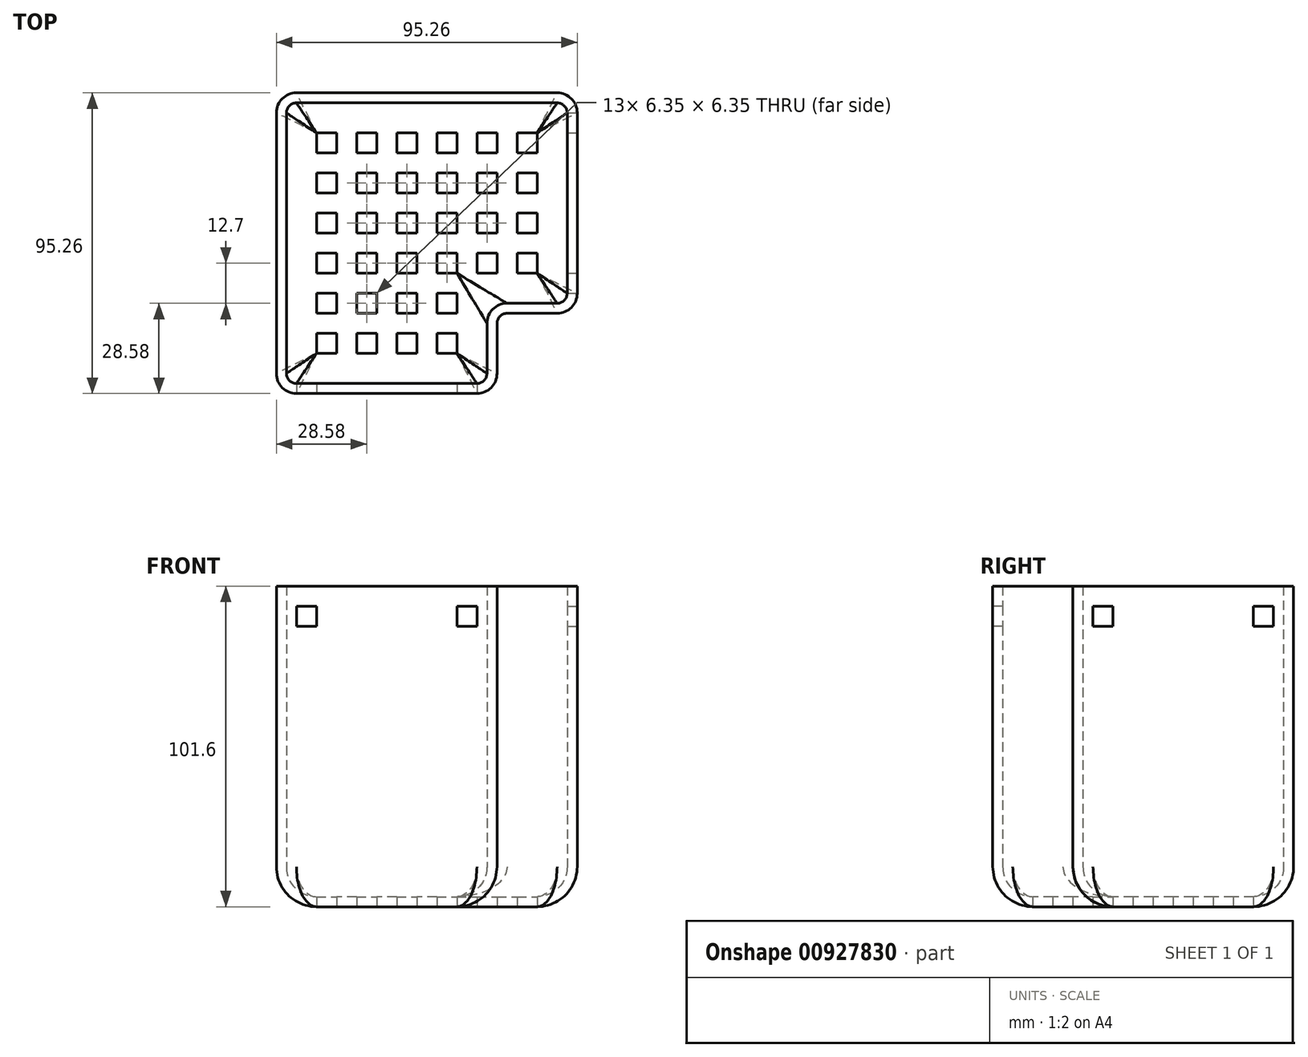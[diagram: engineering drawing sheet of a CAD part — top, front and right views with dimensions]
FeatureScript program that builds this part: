
annotation { "Feature Type Name" : "Feature", "Feature Type Description" : "" }
export const myFeature = defineFeature(function(context is Context, id is Id, definition is map)
    precondition{}
    {
        {
            var Q0;
            Q0=qCreatedBy(makeId("Top.planeOp"),FACE);
            var sketch = newSketch(context, id + "F0", { "sketchPlane" : qUnion([Q0])});
            skLineSegment(sketch, "E0.bottom", {"start": v(47.63, 47.63) * mm, "end": v(-47.63, 47.63) * mm});
            skLineSegment(sketch, "E0.top", {"start": v(22.23, -47.63) * mm, "end": v(-47.63, -47.63) * mm});
            skLineSegment(sketch, "E0.left", {"start": v(47.63, 47.63) * mm, "end": v(47.63, -22.23) * mm});
            skLineSegment(sketch, "E0.right", {"start": v(-47.63, 47.63) * mm, "end": v(-47.63, -47.63) * mm});
            skPoint(sketch, "E0.middle", {"position": v(0, 0) * mm});
            skLineSegment(sketch, "E1", {"start": v(22.23, -47.62) * mm, "end": v(22.23, -22.23) * mm});
            skLineSegment(sketch, "E2", {"start": v(22.23, -22.23) * mm, "end": v(47.62, -22.23) * mm});
            skPoint(sketch, "E3.orphan", {"position": v(47.63, -47.63) * mm});
            skLineSegment(sketch, "E4.0", {"start": v(44.45, 44.45) * mm, "end": v(44.45, -19.05) * mm});
            skLineSegment(sketch, "E4.1", {"start": v(-44.45, 44.45) * mm, "end": v(-44.45, -44.45) * mm});
            skLineSegment(sketch, "E4.2", {"start": v(19.05, -44.45) * mm, "end": v(-44.45, -44.45) * mm});
            skLineSegment(sketch, "E4.3", {"start": v(44.45, 44.45) * mm, "end": v(-44.45, 44.45) * mm});
            skLineSegment(sketch, "E4.4", {"start": v(19.05, -44.45) * mm, "end": v(19.05, -19.05) * mm});
            skLineSegment(sketch, "E4.5", {"start": v(19.05, -19.05) * mm, "end": v(44.45, -19.05) * mm});
            skSolve(sketch);
        }
        {
            var Q0;
            Q0 = qSketchRegion(id + "F0", true);
            extrude(context, id + "F1", {"entities" : qUnion([Q0]), "depth" : 101.6 * mm, "offsetDistance" : 25.4 * mm});
        }
        {
            var Q0;
            Q0=qCreatedBy(makeId("Top.planeOp"),FACE);
            var sketch = newSketch(context, id + "F2", { "sketchPlane" : qUnion([Q0])});
            skLineSegment(sketch, "E5.0.0", {"start": v(-47.63, -47.63) * mm, "end": v(22.23, -47.63) * mm});
            skLineSegment(sketch, "E5.0.1", {"start": v(22.23, -47.63) * mm, "end": v(22.23, -22.23) * mm});
            skLineSegment(sketch, "E5.0.2", {"start": v(22.23, -22.23) * mm, "end": v(47.63, -22.23) * mm});
            skLineSegment(sketch, "E5.0.3", {"start": v(47.63, -22.23) * mm, "end": v(47.63, 47.63) * mm});
            skLineSegment(sketch, "E5.0.4", {"start": v(47.63, 47.63) * mm, "end": v(-47.63, 47.63) * mm});
            skLineSegment(sketch, "E5.0.5", {"start": v(-47.63, 47.63) * mm, "end": v(-47.63, -47.63) * mm});
            skLineSegment(sketch, "E6.bottom", {"start": v(-34.93, 34.93) * mm, "end": v(-28.58, 34.93) * mm});
            skLineSegment(sketch, "E6.top", {"start": v(-34.93, 28.57) * mm, "end": v(-28.58, 28.57) * mm});
            skLineSegment(sketch, "E6.left", {"start": v(-34.93, 34.93) * mm, "end": v(-34.93, 28.58) * mm});
            skLineSegment(sketch, "E6.right", {"start": v(-28.58, 34.93) * mm, "end": v(-28.58, 28.57) * mm});
            skLineSegment(sketch, "E7.1.0.0", {"start": v(-22.23, 34.93) * mm, "end": v(-15.88, 34.93) * mm});
            skLineSegment(sketch, "E7.1.0.1", {"start": v(-22.23, 34.93) * mm, "end": v(-22.23, 28.58) * mm});
            skLineSegment(sketch, "E7.1.0.2", {"start": v(-15.88, 34.93) * mm, "end": v(-15.88, 28.57) * mm});
            skLineSegment(sketch, "E7.1.0.3", {"start": v(-22.23, 28.57) * mm, "end": v(-15.88, 28.57) * mm});
            skLineSegment(sketch, "E7.2.0.0", {"start": v(-9.53, 34.93) * mm, "end": v(-3.18, 34.93) * mm});
            skLineSegment(sketch, "E7.2.0.1", {"start": v(-9.53, 34.93) * mm, "end": v(-9.53, 28.58) * mm});
            skLineSegment(sketch, "E7.2.0.2", {"start": v(-3.18, 34.93) * mm, "end": v(-3.18, 28.57) * mm});
            skLineSegment(sketch, "E7.2.0.3", {"start": v(-9.53, 28.58) * mm, "end": v(-3.18, 28.58) * mm});
            skLineSegment(sketch, "E7.direction1", {"start": v(-34.93, 28.58) * mm, "end": v(-22.23, 28.58) * mm, "construction": true});
            skLineSegment(sketch, "E8.0.3.0", {"start": v(3.17, 34.93) * mm, "end": v(9.52, 34.93) * mm});
            skLineSegment(sketch, "E8.3.3.0", {"start": v(3.17, 34.93) * mm, "end": v(3.17, 28.58) * mm});
            skLineSegment(sketch, "E8.6.3.0", {"start": v(9.52, 34.93) * mm, "end": v(9.52, 28.57) * mm});
            skLineSegment(sketch, "E8.9.3.0", {"start": v(3.17, 28.58) * mm, "end": v(9.52, 28.58) * mm});
            skLineSegment(sketch, "E8.0.4.0", {"start": v(15.87, 34.93) * mm, "end": v(22.22, 34.93) * mm});
            skLineSegment(sketch, "E8.3.4.0", {"start": v(15.87, 34.93) * mm, "end": v(15.87, 28.58) * mm});
            skLineSegment(sketch, "E8.6.4.0", {"start": v(22.22, 34.93) * mm, "end": v(22.22, 28.57) * mm});
            skLineSegment(sketch, "E8.9.4.0", {"start": v(15.87, 28.58) * mm, "end": v(22.22, 28.58) * mm});
            skLineSegment(sketch, "E8.0.5.0", {"start": v(28.57, 34.93) * mm, "end": v(34.92, 34.93) * mm});
            skLineSegment(sketch, "E8.3.5.0", {"start": v(28.57, 34.93) * mm, "end": v(28.57, 28.58) * mm});
            skLineSegment(sketch, "E8.6.5.0", {"start": v(34.92, 34.93) * mm, "end": v(34.92, 28.57) * mm});
            skLineSegment(sketch, "E8.9.5.0", {"start": v(28.57, 28.58) * mm, "end": v(34.92, 28.58) * mm});
            skLineSegment(sketch, "E9.0.1.0", {"start": v(-34.93, 15.88) * mm, "end": v(-22.23, 15.88) * mm, "construction": true});
            skLineSegment(sketch, "E9.0.1.1", {"start": v(-22.23, 15.87) * mm, "end": v(-15.88, 15.87) * mm});
            skLineSegment(sketch, "E9.0.1.2", {"start": v(-28.58, 22.23) * mm, "end": v(-28.58, 15.87) * mm});
            skLineSegment(sketch, "E9.0.1.3", {"start": v(-22.23, 22.23) * mm, "end": v(-22.23, 15.88) * mm});
            skLineSegment(sketch, "E9.0.1.4", {"start": v(3.17, 22.23) * mm, "end": v(9.52, 22.23) * mm});
            skLineSegment(sketch, "E9.0.1.5", {"start": v(-15.88, 22.23) * mm, "end": v(-15.88, 15.87) * mm});
            skLineSegment(sketch, "E9.0.1.6", {"start": v(15.87, 15.88) * mm, "end": v(22.22, 15.88) * mm});
            skLineSegment(sketch, "E9.0.1.7", {"start": v(-34.93, 22.23) * mm, "end": v(-28.58, 22.23) * mm});
            skLineSegment(sketch, "E9.0.1.8", {"start": v(9.52, 22.23) * mm, "end": v(9.52, 15.87) * mm});
            skLineSegment(sketch, "E9.0.1.9", {"start": v(34.92, 22.23) * mm, "end": v(34.92, 15.87) * mm});
            skLineSegment(sketch, "E9.0.1.10", {"start": v(15.87, 22.23) * mm, "end": v(22.22, 22.23) * mm});
            skLineSegment(sketch, "E9.0.1.11", {"start": v(22.22, 22.23) * mm, "end": v(22.22, 15.87) * mm});
            skLineSegment(sketch, "E9.0.1.12", {"start": v(28.57, 22.23) * mm, "end": v(34.92, 22.23) * mm});
            skLineSegment(sketch, "E9.0.1.13", {"start": v(-34.93, 22.23) * mm, "end": v(-34.93, 15.88) * mm});
            skLineSegment(sketch, "E9.0.1.14", {"start": v(-22.23, 22.23) * mm, "end": v(-15.88, 22.23) * mm});
            skLineSegment(sketch, "E9.0.1.15", {"start": v(15.87, 22.23) * mm, "end": v(15.87, 15.88) * mm});
            skLineSegment(sketch, "E9.0.1.16", {"start": v(28.57, 15.88) * mm, "end": v(34.92, 15.88) * mm});
            skLineSegment(sketch, "E9.0.1.17", {"start": v(3.17, 22.23) * mm, "end": v(3.17, 15.88) * mm});
            skLineSegment(sketch, "E9.0.1.18", {"start": v(3.17, 15.88) * mm, "end": v(9.52, 15.88) * mm});
            skLineSegment(sketch, "E9.0.1.19", {"start": v(-9.53, 22.23) * mm, "end": v(-9.53, 15.88) * mm});
            skLineSegment(sketch, "E9.0.1.20", {"start": v(28.57, 22.23) * mm, "end": v(28.57, 15.88) * mm});
            skLineSegment(sketch, "E9.0.1.21", {"start": v(-3.18, 22.23) * mm, "end": v(-3.18, 15.87) * mm});
            skLineSegment(sketch, "E9.0.1.22", {"start": v(-9.53, 22.23) * mm, "end": v(-3.18, 22.23) * mm});
            skLineSegment(sketch, "E9.0.1.23", {"start": v(-9.53, 15.88) * mm, "end": v(-3.18, 15.88) * mm});
            skLineSegment(sketch, "E9.0.1.24", {"start": v(-34.93, 15.87) * mm, "end": v(-28.58, 15.87) * mm});
            skLineSegment(sketch, "E9.0.2.0", {"start": v(-34.93, 3.18) * mm, "end": v(-22.23, 3.18) * mm, "construction": true});
            skLineSegment(sketch, "E9.0.2.1", {"start": v(-22.23, 3.17) * mm, "end": v(-15.88, 3.17) * mm});
            skLineSegment(sketch, "E9.0.2.2", {"start": v(-28.58, 9.53) * mm, "end": v(-28.58, 3.17) * mm});
            skLineSegment(sketch, "E9.0.2.3", {"start": v(-22.23, 9.53) * mm, "end": v(-22.23, 3.18) * mm});
            skLineSegment(sketch, "E9.0.2.4", {"start": v(3.17, 9.53) * mm, "end": v(9.52, 9.53) * mm});
            skLineSegment(sketch, "E9.0.2.5", {"start": v(-15.88, 9.53) * mm, "end": v(-15.88, 3.17) * mm});
            skLineSegment(sketch, "E9.0.2.6", {"start": v(15.87, 3.18) * mm, "end": v(22.22, 3.18) * mm});
            skLineSegment(sketch, "E9.0.2.7", {"start": v(-34.93, 9.53) * mm, "end": v(-28.58, 9.53) * mm});
            skLineSegment(sketch, "E9.0.2.8", {"start": v(9.52, 9.53) * mm, "end": v(9.52, 3.17) * mm});
            skLineSegment(sketch, "E9.0.2.9", {"start": v(34.92, 9.53) * mm, "end": v(34.92, 3.17) * mm});
            skLineSegment(sketch, "E9.0.2.10", {"start": v(15.87, 9.53) * mm, "end": v(22.22, 9.53) * mm});
            skLineSegment(sketch, "E9.0.2.11", {"start": v(22.22, 9.53) * mm, "end": v(22.22, 3.17) * mm});
            skLineSegment(sketch, "E9.0.2.12", {"start": v(28.57, 9.53) * mm, "end": v(34.92, 9.53) * mm});
            skLineSegment(sketch, "E9.0.2.13", {"start": v(-34.93, 9.53) * mm, "end": v(-34.93, 3.18) * mm});
            skLineSegment(sketch, "E9.0.2.14", {"start": v(-22.23, 9.53) * mm, "end": v(-15.88, 9.53) * mm});
            skLineSegment(sketch, "E9.0.2.15", {"start": v(15.87, 9.53) * mm, "end": v(15.87, 3.18) * mm});
            skLineSegment(sketch, "E9.0.2.16", {"start": v(28.57, 3.18) * mm, "end": v(34.92, 3.18) * mm});
            skLineSegment(sketch, "E9.0.2.17", {"start": v(3.17, 9.53) * mm, "end": v(3.17, 3.18) * mm});
            skLineSegment(sketch, "E9.0.2.18", {"start": v(3.17, 3.18) * mm, "end": v(9.52, 3.18) * mm});
            skLineSegment(sketch, "E9.0.2.19", {"start": v(-9.53, 9.53) * mm, "end": v(-9.53, 3.18) * mm});
            skLineSegment(sketch, "E9.0.2.20", {"start": v(28.57, 9.53) * mm, "end": v(28.57, 3.18) * mm});
            skLineSegment(sketch, "E9.0.2.21", {"start": v(-3.18, 9.53) * mm, "end": v(-3.18, 3.17) * mm});
            skLineSegment(sketch, "E9.0.2.22", {"start": v(-9.53, 9.53) * mm, "end": v(-3.18, 9.53) * mm});
            skLineSegment(sketch, "E9.0.2.23", {"start": v(-9.53, 3.18) * mm, "end": v(-3.18, 3.18) * mm});
            skLineSegment(sketch, "E9.0.2.24", {"start": v(-34.93, 3.17) * mm, "end": v(-28.58, 3.17) * mm});
            skLineSegment(sketch, "E9.0.3.0", {"start": v(-34.93, -9.52) * mm, "end": v(-22.23, -9.52) * mm, "construction": true});
            skLineSegment(sketch, "E9.0.3.1", {"start": v(-22.23, -9.53) * mm, "end": v(-15.88, -9.52) * mm});
            skLineSegment(sketch, "E9.0.3.2", {"start": v(-28.58, -3.17) * mm, "end": v(-28.58, -9.53) * mm});
            skLineSegment(sketch, "E9.0.3.3", {"start": v(-22.23, -3.17) * mm, "end": v(-22.23, -9.52) * mm});
            skLineSegment(sketch, "E9.0.3.4", {"start": v(3.17, -3.17) * mm, "end": v(9.52, -3.17) * mm});
            skLineSegment(sketch, "E9.0.3.5", {"start": v(-15.88, -3.17) * mm, "end": v(-15.88, -9.53) * mm});
            skLineSegment(sketch, "E9.0.3.6", {"start": v(15.87, -9.52) * mm, "end": v(22.22, -9.52) * mm});
            skLineSegment(sketch, "E9.0.3.7", {"start": v(-34.93, -3.17) * mm, "end": v(-28.58, -3.17) * mm});
            skLineSegment(sketch, "E9.0.3.8", {"start": v(9.52, -3.17) * mm, "end": v(9.52, -9.53) * mm});
            skLineSegment(sketch, "E9.0.3.9", {"start": v(34.92, -3.17) * mm, "end": v(34.92, -9.53) * mm});
            skLineSegment(sketch, "E9.0.3.10", {"start": v(15.87, -3.17) * mm, "end": v(22.22, -3.17) * mm});
            skLineSegment(sketch, "E9.0.3.11", {"start": v(22.22, -3.17) * mm, "end": v(22.22, -9.53) * mm});
            skLineSegment(sketch, "E9.0.3.12", {"start": v(28.57, -3.17) * mm, "end": v(34.92, -3.17) * mm});
            skLineSegment(sketch, "E9.0.3.13", {"start": v(-34.93, -3.17) * mm, "end": v(-34.93, -9.52) * mm});
            skLineSegment(sketch, "E9.0.3.14", {"start": v(-22.23, -3.17) * mm, "end": v(-15.88, -3.17) * mm});
            skLineSegment(sketch, "E9.0.3.15", {"start": v(15.87, -3.17) * mm, "end": v(15.87, -9.52) * mm});
            skLineSegment(sketch, "E9.0.3.16", {"start": v(28.57, -9.52) * mm, "end": v(34.92, -9.52) * mm});
            skLineSegment(sketch, "E9.0.3.17", {"start": v(3.17, -3.17) * mm, "end": v(3.17, -9.52) * mm});
            skLineSegment(sketch, "E9.0.3.18", {"start": v(3.17, -9.52) * mm, "end": v(9.52, -9.52) * mm});
            skLineSegment(sketch, "E9.0.3.19", {"start": v(-9.53, -3.17) * mm, "end": v(-9.53, -9.52) * mm});
            skLineSegment(sketch, "E9.0.3.20", {"start": v(28.57, -3.17) * mm, "end": v(28.57, -9.52) * mm});
            skLineSegment(sketch, "E9.0.3.21", {"start": v(-3.18, -3.17) * mm, "end": v(-3.18, -9.53) * mm});
            skLineSegment(sketch, "E9.0.3.22", {"start": v(-9.53, -3.17) * mm, "end": v(-3.18, -3.17) * mm});
            skLineSegment(sketch, "E9.0.3.23", {"start": v(-9.53, -9.52) * mm, "end": v(-3.18, -9.52) * mm});
            skLineSegment(sketch, "E9.0.3.24", {"start": v(-34.93, -9.53) * mm, "end": v(-28.58, -9.53) * mm});
            skLineSegment(sketch, "E9.0.4.0", {"start": v(-34.93, -22.22) * mm, "end": v(-22.23, -22.22) * mm, "construction": true});
            skLineSegment(sketch, "E9.0.4.1", {"start": v(-22.23, -22.23) * mm, "end": v(-15.88, -22.23) * mm});
            skLineSegment(sketch, "E9.0.4.2", {"start": v(-28.58, -15.87) * mm, "end": v(-28.58, -22.23) * mm});
            skLineSegment(sketch, "E9.0.4.3", {"start": v(-22.23, -15.87) * mm, "end": v(-22.23, -22.22) * mm});
            skLineSegment(sketch, "E9.0.4.4", {"start": v(3.17, -15.87) * mm, "end": v(9.52, -15.87) * mm});
            skLineSegment(sketch, "E9.0.4.5", {"start": v(-15.88, -15.87) * mm, "end": v(-15.88, -22.23) * mm});
            skLineSegment(sketch, "E9.0.4.7", {"start": v(-34.93, -15.87) * mm, "end": v(-28.58, -15.87) * mm});
            skLineSegment(sketch, "E9.0.4.8", {"start": v(9.52, -15.87) * mm, "end": v(9.52, -22.23) * mm});
            skLineSegment(sketch, "E9.0.4.13", {"start": v(-34.93, -15.87) * mm, "end": v(-34.93, -22.22) * mm});
            skLineSegment(sketch, "E9.0.4.14", {"start": v(-22.23, -15.87) * mm, "end": v(-15.88, -15.87) * mm});
            skLineSegment(sketch, "E9.0.4.17", {"start": v(3.17, -15.87) * mm, "end": v(3.17, -22.22) * mm});
            skLineSegment(sketch, "E9.0.4.18", {"start": v(3.17, -22.22) * mm, "end": v(9.52, -22.22) * mm});
            skLineSegment(sketch, "E9.0.4.19", {"start": v(-9.53, -15.87) * mm, "end": v(-9.53, -22.22) * mm});
            skLineSegment(sketch, "E9.0.4.21", {"start": v(-3.18, -15.87) * mm, "end": v(-3.18, -22.23) * mm});
            skLineSegment(sketch, "E9.0.4.22", {"start": v(-9.53, -15.87) * mm, "end": v(-3.18, -15.87) * mm});
            skLineSegment(sketch, "E9.0.4.23", {"start": v(-9.53, -22.22) * mm, "end": v(-3.18, -22.22) * mm});
            skLineSegment(sketch, "E9.0.4.24", {"start": v(-34.93, -22.23) * mm, "end": v(-28.58, -22.23) * mm});
            skLineSegment(sketch, "E9.0.5.0", {"start": v(-34.93, -34.92) * mm, "end": v(-22.23, -34.92) * mm, "construction": true});
            skLineSegment(sketch, "E9.0.5.1", {"start": v(-22.23, -34.93) * mm, "end": v(-15.88, -34.93) * mm});
            skLineSegment(sketch, "E9.0.5.2", {"start": v(-28.58, -28.57) * mm, "end": v(-28.58, -34.93) * mm});
            skLineSegment(sketch, "E9.0.5.3", {"start": v(-22.23, -28.57) * mm, "end": v(-22.23, -34.92) * mm});
            skLineSegment(sketch, "E9.0.5.4", {"start": v(3.17, -28.57) * mm, "end": v(9.52, -28.57) * mm});
            skLineSegment(sketch, "E9.0.5.5", {"start": v(-15.88, -28.57) * mm, "end": v(-15.88, -34.93) * mm});
            skLineSegment(sketch, "E9.0.5.7", {"start": v(-34.93, -28.57) * mm, "end": v(-28.58, -28.57) * mm});
            skLineSegment(sketch, "E9.0.5.8", {"start": v(9.52, -28.57) * mm, "end": v(9.52, -34.93) * mm});
            skLineSegment(sketch, "E9.0.5.13", {"start": v(-34.93, -28.57) * mm, "end": v(-34.93, -34.92) * mm});
            skLineSegment(sketch, "E9.0.5.14", {"start": v(-22.23, -28.57) * mm, "end": v(-15.88, -28.57) * mm});
            skLineSegment(sketch, "E9.0.5.17", {"start": v(3.17, -28.57) * mm, "end": v(3.17, -34.92) * mm});
            skLineSegment(sketch, "E9.0.5.18", {"start": v(3.17, -34.92) * mm, "end": v(9.52, -34.92) * mm});
            skLineSegment(sketch, "E9.0.5.19", {"start": v(-9.53, -28.57) * mm, "end": v(-9.53, -34.92) * mm});
            skLineSegment(sketch, "E9.0.5.21", {"start": v(-3.18, -28.57) * mm, "end": v(-3.18, -34.93) * mm});
            skLineSegment(sketch, "E9.0.5.22", {"start": v(-9.53, -28.57) * mm, "end": v(-3.18, -28.57) * mm});
            skLineSegment(sketch, "E9.0.5.23", {"start": v(-9.53, -34.92) * mm, "end": v(-3.18, -34.92) * mm});
            skLineSegment(sketch, "E9.0.5.24", {"start": v(-34.93, -34.93) * mm, "end": v(-28.58, -34.93) * mm});
            skLineSegment(sketch, "E9.direction1", {"start": v(-34.93, 28.57) * mm, "end": v(-9.53, 28.57) * mm, "construction": true});
            skLineSegment(sketch, "E9.direction2", {"start": v(-34.93, 28.57) * mm, "end": v(-34.93, 15.87) * mm, "construction": true});
            skSolve(sketch);
        }
        {
            var Q0;
            Q0=makeQuery(id+"F2.imprint","IMPRINT",FACE,{"disambiguationData":[TD([[makeQuery(id+"F2.imprint","IMPRINT",EDGE,{"derivedFrom":sQuery(id+"F2.wireOp",EDGE,"E5.0.0")}),1.0]])]});
            extrude(context, id + "F3", {"entities" : qUnion([Q0]), "operationType" : NewBodyOperationType.ADD, "depth" : 3.17 * mm, "offsetDistance" : 25.4 * mm});
        }
        {
            var Q0;
            Q0=makeQuery(id+"F1.opExtrude","SWEPT_FACE",FACE,{"disambiguationData":[OSD([sQuery(id+"F0.wireOp",EDGE,"E0.top")])]});
            var sketch = newSketch(context, id + "F4", { "sketchPlane" : qUnion([Q0])});
            skLineSegment(sketch, "E10.bottom", {"start": v(-41.28, 95.25) * mm, "end": v(-34.93, 95.25) * mm});
            skLineSegment(sketch, "E10.top", {"start": v(-41.28, 88.9) * mm, "end": v(-34.93, 88.9) * mm});
            skLineSegment(sketch, "E10.left", {"start": v(-41.28, 95.25) * mm, "end": v(-41.28, 88.9) * mm});
            skLineSegment(sketch, "E10.right", {"start": v(-34.93, 95.25) * mm, "end": v(-34.93, 88.9) * mm});
            skLineSegment(sketch, "E11.bottom", {"start": v(15.88, 95.25) * mm, "end": v(9.53, 95.25) * mm});
            skLineSegment(sketch, "E11.top", {"start": v(15.88, 88.9) * mm, "end": v(9.53, 88.9) * mm});
            skLineSegment(sketch, "E11.left", {"start": v(15.88, 95.25) * mm, "end": v(15.88, 88.9) * mm});
            skLineSegment(sketch, "E11.right", {"start": v(9.53, 95.25) * mm, "end": v(9.53, 88.9) * mm});
            skSolve(sketch);
        }
        {
            var Q0;
            Q0 = qSketchRegion(id + "F4", true);
            extrude(context, id + "F5", {"entities" : qUnion([Q0]), "operationType" : NewBodyOperationType.REMOVE, "oppositeDirection" : true, "depth" : 25.4 * mm, "offsetDistance" : 25.4 * mm});
        }
        {
            var Q0;
            Q0=makeQuery(id+"F1.opExtrude","SWEPT_FACE",FACE,{"disambiguationData":[OSD([sQuery(id+"F0.wireOp",EDGE,"E0.left")])]});
            var sketch = newSketch(context, id + "F6", { "sketchPlane" : qUnion([Q0])});
            skLineSegment(sketch, "E12.bottom", {"start": v(41.28, 95.25) * mm, "end": v(34.93, 95.25) * mm});
            skLineSegment(sketch, "E12.top", {"start": v(41.28, 88.9) * mm, "end": v(34.93, 88.9) * mm});
            skLineSegment(sketch, "E12.left", {"start": v(41.28, 95.25) * mm, "end": v(41.28, 88.9) * mm});
            skLineSegment(sketch, "E12.right", {"start": v(34.93, 95.25) * mm, "end": v(34.93, 88.9) * mm});
            skLineSegment(sketch, "E13.bottom", {"start": v(-15.88, 95.25) * mm, "end": v(-9.53, 95.25) * mm});
            skLineSegment(sketch, "E13.top", {"start": v(-15.88, 88.9) * mm, "end": v(-9.53, 88.9) * mm});
            skLineSegment(sketch, "E13.left", {"start": v(-15.88, 95.25) * mm, "end": v(-15.88, 88.9) * mm});
            skLineSegment(sketch, "E13.right", {"start": v(-9.53, 95.25) * mm, "end": v(-9.53, 88.9) * mm});
            skSolve(sketch);
        }
        {
            var Q0;
            Q0 = qSketchRegion(id + "F6", true);
            extrude(context, id + "F7", {"entities" : qUnion([Q0]), "operationType" : NewBodyOperationType.REMOVE, "oppositeDirection" : true, "depth" : 25.4 * mm, "offsetDistance" : 25.4 * mm});
        }
        {
            var Q0;
            Q0=makeQuery(id+"F3.boolean.opBoolean","INTERSECT",EDGE,{"derivedFrom":[makeQuery(id+"F1.opExtrude","SWEPT_FACE",FACE,{"disambiguationData":[OSD([sQuery(id+"F0.wireOp",EDGE,"E4.3")])]}),makeQuery(id+"F3.opExtrude","CAP_FACE",FACE,{"disambiguationData":[OSD([sQuery(id+"F2.wireOp",EDGE,"E5.0.0"),sQuery(id+"F2.wireOp",EDGE,"E5.0.1"),sQuery(id+"F2.wireOp",EDGE,"E5.0.2"),sQuery(id+"F2.wireOp",EDGE,"E5.0.3"),sQuery(id+"F2.wireOp",EDGE,"E5.0.4"),sQuery(id+"F2.wireOp",EDGE,"E5.0.5"),sQuery(id+"F2.wireOp",EDGE,"E6.bottom"),sQuery(id+"F2.wireOp",EDGE,"E6.top"),sQuery(id+"F2.wireOp",EDGE,"E6.left"),sQuery(id+"F2.wireOp",EDGE,"E6.right"),sQuery(id+"F2.wireOp",EDGE,"E7.1.0.0"),sQuery(id+"F2.wireOp",EDGE,"E7.1.0.1"),sQuery(id+"F2.wireOp",EDGE,"E7.1.0.2"),sQuery(id+"F2.wireOp",EDGE,"E7.1.0.3"),sQuery(id+"F2.wireOp",EDGE,"E7.2.0.0"),sQuery(id+"F2.wireOp",EDGE,"E7.2.0.1"),sQuery(id+"F2.wireOp",EDGE,"E7.2.0.2"),sQuery(id+"F2.wireOp",EDGE,"E7.2.0.3"),sQuery(id+"F2.wireOp",EDGE,"E8.0.3.0"),sQuery(id+"F2.wireOp",EDGE,"E8.3.3.0"),sQuery(id+"F2.wireOp",EDGE,"E8.6.3.0"),sQuery(id+"F2.wireOp",EDGE,"E8.9.3.0"),sQuery(id+"F2.wireOp",EDGE,"E8.0.4.0"),sQuery(id+"F2.wireOp",EDGE,"E8.3.4.0"),sQuery(id+"F2.wireOp",EDGE,"E8.6.4.0"),sQuery(id+"F2.wireOp",EDGE,"E8.9.4.0"),sQuery(id+"F2.wireOp",EDGE,"E8.0.5.0"),sQuery(id+"F2.wireOp",EDGE,"E8.3.5.0"),sQuery(id+"F2.wireOp",EDGE,"E8.6.5.0"),sQuery(id+"F2.wireOp",EDGE,"E8.9.5.0"),sQuery(id+"F2.wireOp",EDGE,"E9.0.1.1"),sQuery(id+"F2.wireOp",EDGE,"E9.0.1.2"),sQuery(id+"F2.wireOp",EDGE,"E9.0.1.3"),sQuery(id+"F2.wireOp",EDGE,"E9.0.1.4"),sQuery(id+"F2.wireOp",EDGE,"E9.0.1.5"),sQuery(id+"F2.wireOp",EDGE,"E9.0.1.6"),sQuery(id+"F2.wireOp",EDGE,"E9.0.1.7"),sQuery(id+"F2.wireOp",EDGE,"E9.0.1.8"),sQuery(id+"F2.wireOp",EDGE,"E9.0.1.9"),sQuery(id+"F2.wireOp",EDGE,"E9.0.1.10"),sQuery(id+"F2.wireOp",EDGE,"E9.0.1.11"),sQuery(id+"F2.wireOp",EDGE,"E9.0.1.12"),sQuery(id+"F2.wireOp",EDGE,"E9.0.1.13"),sQuery(id+"F2.wireOp",EDGE,"E9.0.1.14"),sQuery(id+"F2.wireOp",EDGE,"E9.0.1.15"),sQuery(id+"F2.wireOp",EDGE,"E9.0.1.16"),sQuery(id+"F2.wireOp",EDGE,"E9.0.1.17"),sQuery(id+"F2.wireOp",EDGE,"E9.0.1.18"),sQuery(id+"F2.wireOp",EDGE,"E9.0.1.19"),sQuery(id+"F2.wireOp",EDGE,"E9.0.1.20"),sQuery(id+"F2.wireOp",EDGE,"E9.0.1.21"),sQuery(id+"F2.wireOp",EDGE,"E9.0.1.22"),sQuery(id+"F2.wireOp",EDGE,"E9.0.1.23"),sQuery(id+"F2.wireOp",EDGE,"E9.0.1.24"),sQuery(id+"F2.wireOp",EDGE,"E9.0.2.1"),sQuery(id+"F2.wireOp",EDGE,"E9.0.2.2"),sQuery(id+"F2.wireOp",EDGE,"E9.0.2.3"),sQuery(id+"F2.wireOp",EDGE,"E9.0.2.4"),sQuery(id+"F2.wireOp",EDGE,"E9.0.2.5"),sQuery(id+"F2.wireOp",EDGE,"E9.0.2.6"),sQuery(id+"F2.wireOp",EDGE,"E9.0.2.7"),sQuery(id+"F2.wireOp",EDGE,"E9.0.2.8"),sQuery(id+"F2.wireOp",EDGE,"E9.0.2.9"),sQuery(id+"F2.wireOp",EDGE,"E9.0.2.10"),sQuery(id+"F2.wireOp",EDGE,"E9.0.2.11"),sQuery(id+"F2.wireOp",EDGE,"E9.0.2.12"),sQuery(id+"F2.wireOp",EDGE,"E9.0.2.13"),sQuery(id+"F2.wireOp",EDGE,"E9.0.2.14"),sQuery(id+"F2.wireOp",EDGE,"E9.0.2.15"),sQuery(id+"F2.wireOp",EDGE,"E9.0.2.16"),sQuery(id+"F2.wireOp",EDGE,"E9.0.2.17"),sQuery(id+"F2.wireOp",EDGE,"E9.0.2.18"),sQuery(id+"F2.wireOp",EDGE,"E9.0.2.19"),sQuery(id+"F2.wireOp",EDGE,"E9.0.2.20"),sQuery(id+"F2.wireOp",EDGE,"E9.0.2.21"),sQuery(id+"F2.wireOp",EDGE,"E9.0.2.22"),sQuery(id+"F2.wireOp",EDGE,"E9.0.2.23"),sQuery(id+"F2.wireOp",EDGE,"E9.0.2.24"),sQuery(id+"F2.wireOp",EDGE,"E9.0.3.1"),sQuery(id+"F2.wireOp",EDGE,"E9.0.3.2"),sQuery(id+"F2.wireOp",EDGE,"E9.0.3.3"),sQuery(id+"F2.wireOp",EDGE,"E9.0.3.4"),sQuery(id+"F2.wireOp",EDGE,"E9.0.3.5"),sQuery(id+"F2.wireOp",EDGE,"E9.0.3.6"),sQuery(id+"F2.wireOp",EDGE,"E9.0.3.7"),sQuery(id+"F2.wireOp",EDGE,"E9.0.3.8"),sQuery(id+"F2.wireOp",EDGE,"E9.0.3.9"),sQuery(id+"F2.wireOp",EDGE,"E9.0.3.10"),sQuery(id+"F2.wireOp",EDGE,"E9.0.3.11"),sQuery(id+"F2.wireOp",EDGE,"E9.0.3.12"),sQuery(id+"F2.wireOp",EDGE,"E9.0.3.13"),sQuery(id+"F2.wireOp",EDGE,"E9.0.3.14"),sQuery(id+"F2.wireOp",EDGE,"E9.0.3.15"),sQuery(id+"F2.wireOp",EDGE,"E9.0.3.16"),sQuery(id+"F2.wireOp",EDGE,"E9.0.3.17"),sQuery(id+"F2.wireOp",EDGE,"E9.0.3.18"),sQuery(id+"F2.wireOp",EDGE,"E9.0.3.19"),sQuery(id+"F2.wireOp",EDGE,"E9.0.3.20"),sQuery(id+"F2.wireOp",EDGE,"E9.0.3.21"),sQuery(id+"F2.wireOp",EDGE,"E9.0.3.22"),sQuery(id+"F2.wireOp",EDGE,"E9.0.3.23"),sQuery(id+"F2.wireOp",EDGE,"E9.0.3.24"),sQuery(id+"F2.wireOp",EDGE,"E9.0.4.1"),sQuery(id+"F2.wireOp",EDGE,"E9.0.4.2"),sQuery(id+"F2.wireOp",EDGE,"E9.0.4.3"),sQuery(id+"F2.wireOp",EDGE,"E9.0.4.4"),sQuery(id+"F2.wireOp",EDGE,"E9.0.4.5"),sQuery(id+"F2.wireOp",EDGE,"E9.0.4.7"),sQuery(id+"F2.wireOp",EDGE,"E9.0.4.8"),sQuery(id+"F2.wireOp",EDGE,"E9.0.4.13"),sQuery(id+"F2.wireOp",EDGE,"E9.0.4.14"),sQuery(id+"F2.wireOp",EDGE,"E9.0.4.17"),sQuery(id+"F2.wireOp",EDGE,"E9.0.4.18"),sQuery(id+"F2.wireOp",EDGE,"E9.0.4.19"),sQuery(id+"F2.wireOp",EDGE,"E9.0.4.21"),sQuery(id+"F2.wireOp",EDGE,"E9.0.4.22"),sQuery(id+"F2.wireOp",EDGE,"E9.0.4.23"),sQuery(id+"F2.wireOp",EDGE,"E9.0.4.24"),sQuery(id+"F2.wireOp",EDGE,"E9.0.5.1"),sQuery(id+"F2.wireOp",EDGE,"E9.0.5.2"),sQuery(id+"F2.wireOp",EDGE,"E9.0.5.3"),sQuery(id+"F2.wireOp",EDGE,"E9.0.5.4"),sQuery(id+"F2.wireOp",EDGE,"E9.0.5.5"),sQuery(id+"F2.wireOp",EDGE,"E9.0.5.7"),sQuery(id+"F2.wireOp",EDGE,"E9.0.5.8"),sQuery(id+"F2.wireOp",EDGE,"E9.0.5.13"),sQuery(id+"F2.wireOp",EDGE,"E9.0.5.14"),sQuery(id+"F2.wireOp",EDGE,"E9.0.5.17"),sQuery(id+"F2.wireOp",EDGE,"E9.0.5.18"),sQuery(id+"F2.wireOp",EDGE,"E9.0.5.19"),sQuery(id+"F2.wireOp",EDGE,"E9.0.5.21"),sQuery(id+"F2.wireOp",EDGE,"E9.0.5.22"),sQuery(id+"F2.wireOp",EDGE,"E9.0.5.23"),sQuery(id+"F2.wireOp",EDGE,"E9.0.5.24")])],"isStart":false})]});
            var Q1;
            Q1=makeQuery(id+"F3.boolean.opBoolean","INTERSECT",EDGE,{"derivedFrom":[makeQuery(id+"F1.opExtrude","SWEPT_FACE",FACE,{"disambiguationData":[OSD([sQuery(id+"F0.wireOp",EDGE,"E4.1")])]}),makeQuery(id+"F3.opExtrude","CAP_FACE",FACE,{"disambiguationData":[OSD([sQuery(id+"F2.wireOp",EDGE,"E5.0.0"),sQuery(id+"F2.wireOp",EDGE,"E5.0.1"),sQuery(id+"F2.wireOp",EDGE,"E5.0.2"),sQuery(id+"F2.wireOp",EDGE,"E5.0.3"),sQuery(id+"F2.wireOp",EDGE,"E5.0.4"),sQuery(id+"F2.wireOp",EDGE,"E5.0.5"),sQuery(id+"F2.wireOp",EDGE,"E6.bottom"),sQuery(id+"F2.wireOp",EDGE,"E6.top"),sQuery(id+"F2.wireOp",EDGE,"E6.left"),sQuery(id+"F2.wireOp",EDGE,"E6.right"),sQuery(id+"F2.wireOp",EDGE,"E7.1.0.0"),sQuery(id+"F2.wireOp",EDGE,"E7.1.0.1"),sQuery(id+"F2.wireOp",EDGE,"E7.1.0.2"),sQuery(id+"F2.wireOp",EDGE,"E7.1.0.3"),sQuery(id+"F2.wireOp",EDGE,"E7.2.0.0"),sQuery(id+"F2.wireOp",EDGE,"E7.2.0.1"),sQuery(id+"F2.wireOp",EDGE,"E7.2.0.2"),sQuery(id+"F2.wireOp",EDGE,"E7.2.0.3"),sQuery(id+"F2.wireOp",EDGE,"E8.0.3.0"),sQuery(id+"F2.wireOp",EDGE,"E8.3.3.0"),sQuery(id+"F2.wireOp",EDGE,"E8.6.3.0"),sQuery(id+"F2.wireOp",EDGE,"E8.9.3.0"),sQuery(id+"F2.wireOp",EDGE,"E8.0.4.0"),sQuery(id+"F2.wireOp",EDGE,"E8.3.4.0"),sQuery(id+"F2.wireOp",EDGE,"E8.6.4.0"),sQuery(id+"F2.wireOp",EDGE,"E8.9.4.0"),sQuery(id+"F2.wireOp",EDGE,"E8.0.5.0"),sQuery(id+"F2.wireOp",EDGE,"E8.3.5.0"),sQuery(id+"F2.wireOp",EDGE,"E8.6.5.0"),sQuery(id+"F2.wireOp",EDGE,"E8.9.5.0"),sQuery(id+"F2.wireOp",EDGE,"E9.0.1.1"),sQuery(id+"F2.wireOp",EDGE,"E9.0.1.2"),sQuery(id+"F2.wireOp",EDGE,"E9.0.1.3"),sQuery(id+"F2.wireOp",EDGE,"E9.0.1.4"),sQuery(id+"F2.wireOp",EDGE,"E9.0.1.5"),sQuery(id+"F2.wireOp",EDGE,"E9.0.1.6"),sQuery(id+"F2.wireOp",EDGE,"E9.0.1.7"),sQuery(id+"F2.wireOp",EDGE,"E9.0.1.8"),sQuery(id+"F2.wireOp",EDGE,"E9.0.1.9"),sQuery(id+"F2.wireOp",EDGE,"E9.0.1.10"),sQuery(id+"F2.wireOp",EDGE,"E9.0.1.11"),sQuery(id+"F2.wireOp",EDGE,"E9.0.1.12"),sQuery(id+"F2.wireOp",EDGE,"E9.0.1.13"),sQuery(id+"F2.wireOp",EDGE,"E9.0.1.14"),sQuery(id+"F2.wireOp",EDGE,"E9.0.1.15"),sQuery(id+"F2.wireOp",EDGE,"E9.0.1.16"),sQuery(id+"F2.wireOp",EDGE,"E9.0.1.17"),sQuery(id+"F2.wireOp",EDGE,"E9.0.1.18"),sQuery(id+"F2.wireOp",EDGE,"E9.0.1.19"),sQuery(id+"F2.wireOp",EDGE,"E9.0.1.20"),sQuery(id+"F2.wireOp",EDGE,"E9.0.1.21"),sQuery(id+"F2.wireOp",EDGE,"E9.0.1.22"),sQuery(id+"F2.wireOp",EDGE,"E9.0.1.23"),sQuery(id+"F2.wireOp",EDGE,"E9.0.1.24"),sQuery(id+"F2.wireOp",EDGE,"E9.0.2.1"),sQuery(id+"F2.wireOp",EDGE,"E9.0.2.2"),sQuery(id+"F2.wireOp",EDGE,"E9.0.2.3"),sQuery(id+"F2.wireOp",EDGE,"E9.0.2.4"),sQuery(id+"F2.wireOp",EDGE,"E9.0.2.5"),sQuery(id+"F2.wireOp",EDGE,"E9.0.2.6"),sQuery(id+"F2.wireOp",EDGE,"E9.0.2.7"),sQuery(id+"F2.wireOp",EDGE,"E9.0.2.8"),sQuery(id+"F2.wireOp",EDGE,"E9.0.2.9"),sQuery(id+"F2.wireOp",EDGE,"E9.0.2.10"),sQuery(id+"F2.wireOp",EDGE,"E9.0.2.11"),sQuery(id+"F2.wireOp",EDGE,"E9.0.2.12"),sQuery(id+"F2.wireOp",EDGE,"E9.0.2.13"),sQuery(id+"F2.wireOp",EDGE,"E9.0.2.14"),sQuery(id+"F2.wireOp",EDGE,"E9.0.2.15"),sQuery(id+"F2.wireOp",EDGE,"E9.0.2.16"),sQuery(id+"F2.wireOp",EDGE,"E9.0.2.17"),sQuery(id+"F2.wireOp",EDGE,"E9.0.2.18"),sQuery(id+"F2.wireOp",EDGE,"E9.0.2.19"),sQuery(id+"F2.wireOp",EDGE,"E9.0.2.20"),sQuery(id+"F2.wireOp",EDGE,"E9.0.2.21"),sQuery(id+"F2.wireOp",EDGE,"E9.0.2.22"),sQuery(id+"F2.wireOp",EDGE,"E9.0.2.23"),sQuery(id+"F2.wireOp",EDGE,"E9.0.2.24"),sQuery(id+"F2.wireOp",EDGE,"E9.0.3.1"),sQuery(id+"F2.wireOp",EDGE,"E9.0.3.2"),sQuery(id+"F2.wireOp",EDGE,"E9.0.3.3"),sQuery(id+"F2.wireOp",EDGE,"E9.0.3.4"),sQuery(id+"F2.wireOp",EDGE,"E9.0.3.5"),sQuery(id+"F2.wireOp",EDGE,"E9.0.3.6"),sQuery(id+"F2.wireOp",EDGE,"E9.0.3.7"),sQuery(id+"F2.wireOp",EDGE,"E9.0.3.8"),sQuery(id+"F2.wireOp",EDGE,"E9.0.3.9"),sQuery(id+"F2.wireOp",EDGE,"E9.0.3.10"),sQuery(id+"F2.wireOp",EDGE,"E9.0.3.11"),sQuery(id+"F2.wireOp",EDGE,"E9.0.3.12"),sQuery(id+"F2.wireOp",EDGE,"E9.0.3.13"),sQuery(id+"F2.wireOp",EDGE,"E9.0.3.14"),sQuery(id+"F2.wireOp",EDGE,"E9.0.3.15"),sQuery(id+"F2.wireOp",EDGE,"E9.0.3.16"),sQuery(id+"F2.wireOp",EDGE,"E9.0.3.17"),sQuery(id+"F2.wireOp",EDGE,"E9.0.3.18"),sQuery(id+"F2.wireOp",EDGE,"E9.0.3.19"),sQuery(id+"F2.wireOp",EDGE,"E9.0.3.20"),sQuery(id+"F2.wireOp",EDGE,"E9.0.3.21"),sQuery(id+"F2.wireOp",EDGE,"E9.0.3.22"),sQuery(id+"F2.wireOp",EDGE,"E9.0.3.23"),sQuery(id+"F2.wireOp",EDGE,"E9.0.3.24"),sQuery(id+"F2.wireOp",EDGE,"E9.0.4.1"),sQuery(id+"F2.wireOp",EDGE,"E9.0.4.2"),sQuery(id+"F2.wireOp",EDGE,"E9.0.4.3"),sQuery(id+"F2.wireOp",EDGE,"E9.0.4.4"),sQuery(id+"F2.wireOp",EDGE,"E9.0.4.5"),sQuery(id+"F2.wireOp",EDGE,"E9.0.4.7"),sQuery(id+"F2.wireOp",EDGE,"E9.0.4.8"),sQuery(id+"F2.wireOp",EDGE,"E9.0.4.13"),sQuery(id+"F2.wireOp",EDGE,"E9.0.4.14"),sQuery(id+"F2.wireOp",EDGE,"E9.0.4.17"),sQuery(id+"F2.wireOp",EDGE,"E9.0.4.18"),sQuery(id+"F2.wireOp",EDGE,"E9.0.4.19"),sQuery(id+"F2.wireOp",EDGE,"E9.0.4.21"),sQuery(id+"F2.wireOp",EDGE,"E9.0.4.22"),sQuery(id+"F2.wireOp",EDGE,"E9.0.4.23"),sQuery(id+"F2.wireOp",EDGE,"E9.0.4.24"),sQuery(id+"F2.wireOp",EDGE,"E9.0.5.1"),sQuery(id+"F2.wireOp",EDGE,"E9.0.5.2"),sQuery(id+"F2.wireOp",EDGE,"E9.0.5.3"),sQuery(id+"F2.wireOp",EDGE,"E9.0.5.4"),sQuery(id+"F2.wireOp",EDGE,"E9.0.5.5"),sQuery(id+"F2.wireOp",EDGE,"E9.0.5.7"),sQuery(id+"F2.wireOp",EDGE,"E9.0.5.8"),sQuery(id+"F2.wireOp",EDGE,"E9.0.5.13"),sQuery(id+"F2.wireOp",EDGE,"E9.0.5.14"),sQuery(id+"F2.wireOp",EDGE,"E9.0.5.17"),sQuery(id+"F2.wireOp",EDGE,"E9.0.5.18"),sQuery(id+"F2.wireOp",EDGE,"E9.0.5.19"),sQuery(id+"F2.wireOp",EDGE,"E9.0.5.21"),sQuery(id+"F2.wireOp",EDGE,"E9.0.5.22"),sQuery(id+"F2.wireOp",EDGE,"E9.0.5.23"),sQuery(id+"F2.wireOp",EDGE,"E9.0.5.24")])],"isStart":false})]});
            var Q2;
            Q2=makeQuery(id+"F3.boolean.opBoolean","INTERSECT",EDGE,{"derivedFrom":[makeQuery(id+"F1.opExtrude","SWEPT_FACE",FACE,{"disambiguationData":[OSD([sQuery(id+"F0.wireOp",EDGE,"E4.0")])]}),makeQuery(id+"F3.opExtrude","CAP_FACE",FACE,{"disambiguationData":[OSD([sQuery(id+"F2.wireOp",EDGE,"E5.0.0"),sQuery(id+"F2.wireOp",EDGE,"E5.0.1"),sQuery(id+"F2.wireOp",EDGE,"E5.0.2"),sQuery(id+"F2.wireOp",EDGE,"E5.0.3"),sQuery(id+"F2.wireOp",EDGE,"E5.0.4"),sQuery(id+"F2.wireOp",EDGE,"E5.0.5"),sQuery(id+"F2.wireOp",EDGE,"E6.bottom"),sQuery(id+"F2.wireOp",EDGE,"E6.top"),sQuery(id+"F2.wireOp",EDGE,"E6.left"),sQuery(id+"F2.wireOp",EDGE,"E6.right"),sQuery(id+"F2.wireOp",EDGE,"E7.1.0.0"),sQuery(id+"F2.wireOp",EDGE,"E7.1.0.1"),sQuery(id+"F2.wireOp",EDGE,"E7.1.0.2"),sQuery(id+"F2.wireOp",EDGE,"E7.1.0.3"),sQuery(id+"F2.wireOp",EDGE,"E7.2.0.0"),sQuery(id+"F2.wireOp",EDGE,"E7.2.0.1"),sQuery(id+"F2.wireOp",EDGE,"E7.2.0.2"),sQuery(id+"F2.wireOp",EDGE,"E7.2.0.3"),sQuery(id+"F2.wireOp",EDGE,"E8.0.3.0"),sQuery(id+"F2.wireOp",EDGE,"E8.3.3.0"),sQuery(id+"F2.wireOp",EDGE,"E8.6.3.0"),sQuery(id+"F2.wireOp",EDGE,"E8.9.3.0"),sQuery(id+"F2.wireOp",EDGE,"E8.0.4.0"),sQuery(id+"F2.wireOp",EDGE,"E8.3.4.0"),sQuery(id+"F2.wireOp",EDGE,"E8.6.4.0"),sQuery(id+"F2.wireOp",EDGE,"E8.9.4.0"),sQuery(id+"F2.wireOp",EDGE,"E8.0.5.0"),sQuery(id+"F2.wireOp",EDGE,"E8.3.5.0"),sQuery(id+"F2.wireOp",EDGE,"E8.6.5.0"),sQuery(id+"F2.wireOp",EDGE,"E8.9.5.0"),sQuery(id+"F2.wireOp",EDGE,"E9.0.1.1"),sQuery(id+"F2.wireOp",EDGE,"E9.0.1.2"),sQuery(id+"F2.wireOp",EDGE,"E9.0.1.3"),sQuery(id+"F2.wireOp",EDGE,"E9.0.1.4"),sQuery(id+"F2.wireOp",EDGE,"E9.0.1.5"),sQuery(id+"F2.wireOp",EDGE,"E9.0.1.6"),sQuery(id+"F2.wireOp",EDGE,"E9.0.1.7"),sQuery(id+"F2.wireOp",EDGE,"E9.0.1.8"),sQuery(id+"F2.wireOp",EDGE,"E9.0.1.9"),sQuery(id+"F2.wireOp",EDGE,"E9.0.1.10"),sQuery(id+"F2.wireOp",EDGE,"E9.0.1.11"),sQuery(id+"F2.wireOp",EDGE,"E9.0.1.12"),sQuery(id+"F2.wireOp",EDGE,"E9.0.1.13"),sQuery(id+"F2.wireOp",EDGE,"E9.0.1.14"),sQuery(id+"F2.wireOp",EDGE,"E9.0.1.15"),sQuery(id+"F2.wireOp",EDGE,"E9.0.1.16"),sQuery(id+"F2.wireOp",EDGE,"E9.0.1.17"),sQuery(id+"F2.wireOp",EDGE,"E9.0.1.18"),sQuery(id+"F2.wireOp",EDGE,"E9.0.1.19"),sQuery(id+"F2.wireOp",EDGE,"E9.0.1.20"),sQuery(id+"F2.wireOp",EDGE,"E9.0.1.21"),sQuery(id+"F2.wireOp",EDGE,"E9.0.1.22"),sQuery(id+"F2.wireOp",EDGE,"E9.0.1.23"),sQuery(id+"F2.wireOp",EDGE,"E9.0.1.24"),sQuery(id+"F2.wireOp",EDGE,"E9.0.2.1"),sQuery(id+"F2.wireOp",EDGE,"E9.0.2.2"),sQuery(id+"F2.wireOp",EDGE,"E9.0.2.3"),sQuery(id+"F2.wireOp",EDGE,"E9.0.2.4"),sQuery(id+"F2.wireOp",EDGE,"E9.0.2.5"),sQuery(id+"F2.wireOp",EDGE,"E9.0.2.6"),sQuery(id+"F2.wireOp",EDGE,"E9.0.2.7"),sQuery(id+"F2.wireOp",EDGE,"E9.0.2.8"),sQuery(id+"F2.wireOp",EDGE,"E9.0.2.9"),sQuery(id+"F2.wireOp",EDGE,"E9.0.2.10"),sQuery(id+"F2.wireOp",EDGE,"E9.0.2.11"),sQuery(id+"F2.wireOp",EDGE,"E9.0.2.12"),sQuery(id+"F2.wireOp",EDGE,"E9.0.2.13"),sQuery(id+"F2.wireOp",EDGE,"E9.0.2.14"),sQuery(id+"F2.wireOp",EDGE,"E9.0.2.15"),sQuery(id+"F2.wireOp",EDGE,"E9.0.2.16"),sQuery(id+"F2.wireOp",EDGE,"E9.0.2.17"),sQuery(id+"F2.wireOp",EDGE,"E9.0.2.18"),sQuery(id+"F2.wireOp",EDGE,"E9.0.2.19"),sQuery(id+"F2.wireOp",EDGE,"E9.0.2.20"),sQuery(id+"F2.wireOp",EDGE,"E9.0.2.21"),sQuery(id+"F2.wireOp",EDGE,"E9.0.2.22"),sQuery(id+"F2.wireOp",EDGE,"E9.0.2.23"),sQuery(id+"F2.wireOp",EDGE,"E9.0.2.24"),sQuery(id+"F2.wireOp",EDGE,"E9.0.3.1"),sQuery(id+"F2.wireOp",EDGE,"E9.0.3.2"),sQuery(id+"F2.wireOp",EDGE,"E9.0.3.3"),sQuery(id+"F2.wireOp",EDGE,"E9.0.3.4"),sQuery(id+"F2.wireOp",EDGE,"E9.0.3.5"),sQuery(id+"F2.wireOp",EDGE,"E9.0.3.6"),sQuery(id+"F2.wireOp",EDGE,"E9.0.3.7"),sQuery(id+"F2.wireOp",EDGE,"E9.0.3.8"),sQuery(id+"F2.wireOp",EDGE,"E9.0.3.9"),sQuery(id+"F2.wireOp",EDGE,"E9.0.3.10"),sQuery(id+"F2.wireOp",EDGE,"E9.0.3.11"),sQuery(id+"F2.wireOp",EDGE,"E9.0.3.12"),sQuery(id+"F2.wireOp",EDGE,"E9.0.3.13"),sQuery(id+"F2.wireOp",EDGE,"E9.0.3.14"),sQuery(id+"F2.wireOp",EDGE,"E9.0.3.15"),sQuery(id+"F2.wireOp",EDGE,"E9.0.3.16"),sQuery(id+"F2.wireOp",EDGE,"E9.0.3.17"),sQuery(id+"F2.wireOp",EDGE,"E9.0.3.18"),sQuery(id+"F2.wireOp",EDGE,"E9.0.3.19"),sQuery(id+"F2.wireOp",EDGE,"E9.0.3.20"),sQuery(id+"F2.wireOp",EDGE,"E9.0.3.21"),sQuery(id+"F2.wireOp",EDGE,"E9.0.3.22"),sQuery(id+"F2.wireOp",EDGE,"E9.0.3.23"),sQuery(id+"F2.wireOp",EDGE,"E9.0.3.24"),sQuery(id+"F2.wireOp",EDGE,"E9.0.4.1"),sQuery(id+"F2.wireOp",EDGE,"E9.0.4.2"),sQuery(id+"F2.wireOp",EDGE,"E9.0.4.3"),sQuery(id+"F2.wireOp",EDGE,"E9.0.4.4"),sQuery(id+"F2.wireOp",EDGE,"E9.0.4.5"),sQuery(id+"F2.wireOp",EDGE,"E9.0.4.7"),sQuery(id+"F2.wireOp",EDGE,"E9.0.4.8"),sQuery(id+"F2.wireOp",EDGE,"E9.0.4.13"),sQuery(id+"F2.wireOp",EDGE,"E9.0.4.14"),sQuery(id+"F2.wireOp",EDGE,"E9.0.4.17"),sQuery(id+"F2.wireOp",EDGE,"E9.0.4.18"),sQuery(id+"F2.wireOp",EDGE,"E9.0.4.19"),sQuery(id+"F2.wireOp",EDGE,"E9.0.4.21"),sQuery(id+"F2.wireOp",EDGE,"E9.0.4.22"),sQuery(id+"F2.wireOp",EDGE,"E9.0.4.23"),sQuery(id+"F2.wireOp",EDGE,"E9.0.4.24"),sQuery(id+"F2.wireOp",EDGE,"E9.0.5.1"),sQuery(id+"F2.wireOp",EDGE,"E9.0.5.2"),sQuery(id+"F2.wireOp",EDGE,"E9.0.5.3"),sQuery(id+"F2.wireOp",EDGE,"E9.0.5.4"),sQuery(id+"F2.wireOp",EDGE,"E9.0.5.5"),sQuery(id+"F2.wireOp",EDGE,"E9.0.5.7"),sQuery(id+"F2.wireOp",EDGE,"E9.0.5.8"),sQuery(id+"F2.wireOp",EDGE,"E9.0.5.13"),sQuery(id+"F2.wireOp",EDGE,"E9.0.5.14"),sQuery(id+"F2.wireOp",EDGE,"E9.0.5.17"),sQuery(id+"F2.wireOp",EDGE,"E9.0.5.18"),sQuery(id+"F2.wireOp",EDGE,"E9.0.5.19"),sQuery(id+"F2.wireOp",EDGE,"E9.0.5.21"),sQuery(id+"F2.wireOp",EDGE,"E9.0.5.22"),sQuery(id+"F2.wireOp",EDGE,"E9.0.5.23"),sQuery(id+"F2.wireOp",EDGE,"E9.0.5.24")])],"isStart":false})]});
            var Q3;
            Q3=makeQuery(id+"F3.boolean.opBoolean","INTERSECT",EDGE,{"derivedFrom":[makeQuery(id+"F1.opExtrude","SWEPT_FACE",FACE,{"disambiguationData":[OSD([sQuery(id+"F0.wireOp",EDGE,"E4.5")])]}),makeQuery(id+"F3.opExtrude","CAP_FACE",FACE,{"disambiguationData":[OSD([sQuery(id+"F2.wireOp",EDGE,"E5.0.0"),sQuery(id+"F2.wireOp",EDGE,"E5.0.1"),sQuery(id+"F2.wireOp",EDGE,"E5.0.2"),sQuery(id+"F2.wireOp",EDGE,"E5.0.3"),sQuery(id+"F2.wireOp",EDGE,"E5.0.4"),sQuery(id+"F2.wireOp",EDGE,"E5.0.5"),sQuery(id+"F2.wireOp",EDGE,"E6.bottom"),sQuery(id+"F2.wireOp",EDGE,"E6.top"),sQuery(id+"F2.wireOp",EDGE,"E6.left"),sQuery(id+"F2.wireOp",EDGE,"E6.right"),sQuery(id+"F2.wireOp",EDGE,"E7.1.0.0"),sQuery(id+"F2.wireOp",EDGE,"E7.1.0.1"),sQuery(id+"F2.wireOp",EDGE,"E7.1.0.2"),sQuery(id+"F2.wireOp",EDGE,"E7.1.0.3"),sQuery(id+"F2.wireOp",EDGE,"E7.2.0.0"),sQuery(id+"F2.wireOp",EDGE,"E7.2.0.1"),sQuery(id+"F2.wireOp",EDGE,"E7.2.0.2"),sQuery(id+"F2.wireOp",EDGE,"E7.2.0.3"),sQuery(id+"F2.wireOp",EDGE,"E8.0.3.0"),sQuery(id+"F2.wireOp",EDGE,"E8.3.3.0"),sQuery(id+"F2.wireOp",EDGE,"E8.6.3.0"),sQuery(id+"F2.wireOp",EDGE,"E8.9.3.0"),sQuery(id+"F2.wireOp",EDGE,"E8.0.4.0"),sQuery(id+"F2.wireOp",EDGE,"E8.3.4.0"),sQuery(id+"F2.wireOp",EDGE,"E8.6.4.0"),sQuery(id+"F2.wireOp",EDGE,"E8.9.4.0"),sQuery(id+"F2.wireOp",EDGE,"E8.0.5.0"),sQuery(id+"F2.wireOp",EDGE,"E8.3.5.0"),sQuery(id+"F2.wireOp",EDGE,"E8.6.5.0"),sQuery(id+"F2.wireOp",EDGE,"E8.9.5.0"),sQuery(id+"F2.wireOp",EDGE,"E9.0.1.1"),sQuery(id+"F2.wireOp",EDGE,"E9.0.1.2"),sQuery(id+"F2.wireOp",EDGE,"E9.0.1.3"),sQuery(id+"F2.wireOp",EDGE,"E9.0.1.4"),sQuery(id+"F2.wireOp",EDGE,"E9.0.1.5"),sQuery(id+"F2.wireOp",EDGE,"E9.0.1.6"),sQuery(id+"F2.wireOp",EDGE,"E9.0.1.7"),sQuery(id+"F2.wireOp",EDGE,"E9.0.1.8"),sQuery(id+"F2.wireOp",EDGE,"E9.0.1.9"),sQuery(id+"F2.wireOp",EDGE,"E9.0.1.10"),sQuery(id+"F2.wireOp",EDGE,"E9.0.1.11"),sQuery(id+"F2.wireOp",EDGE,"E9.0.1.12"),sQuery(id+"F2.wireOp",EDGE,"E9.0.1.13"),sQuery(id+"F2.wireOp",EDGE,"E9.0.1.14"),sQuery(id+"F2.wireOp",EDGE,"E9.0.1.15"),sQuery(id+"F2.wireOp",EDGE,"E9.0.1.16"),sQuery(id+"F2.wireOp",EDGE,"E9.0.1.17"),sQuery(id+"F2.wireOp",EDGE,"E9.0.1.18"),sQuery(id+"F2.wireOp",EDGE,"E9.0.1.19"),sQuery(id+"F2.wireOp",EDGE,"E9.0.1.20"),sQuery(id+"F2.wireOp",EDGE,"E9.0.1.21"),sQuery(id+"F2.wireOp",EDGE,"E9.0.1.22"),sQuery(id+"F2.wireOp",EDGE,"E9.0.1.23"),sQuery(id+"F2.wireOp",EDGE,"E9.0.1.24"),sQuery(id+"F2.wireOp",EDGE,"E9.0.2.1"),sQuery(id+"F2.wireOp",EDGE,"E9.0.2.2"),sQuery(id+"F2.wireOp",EDGE,"E9.0.2.3"),sQuery(id+"F2.wireOp",EDGE,"E9.0.2.4"),sQuery(id+"F2.wireOp",EDGE,"E9.0.2.5"),sQuery(id+"F2.wireOp",EDGE,"E9.0.2.6"),sQuery(id+"F2.wireOp",EDGE,"E9.0.2.7"),sQuery(id+"F2.wireOp",EDGE,"E9.0.2.8"),sQuery(id+"F2.wireOp",EDGE,"E9.0.2.9"),sQuery(id+"F2.wireOp",EDGE,"E9.0.2.10"),sQuery(id+"F2.wireOp",EDGE,"E9.0.2.11"),sQuery(id+"F2.wireOp",EDGE,"E9.0.2.12"),sQuery(id+"F2.wireOp",EDGE,"E9.0.2.13"),sQuery(id+"F2.wireOp",EDGE,"E9.0.2.14"),sQuery(id+"F2.wireOp",EDGE,"E9.0.2.15"),sQuery(id+"F2.wireOp",EDGE,"E9.0.2.16"),sQuery(id+"F2.wireOp",EDGE,"E9.0.2.17"),sQuery(id+"F2.wireOp",EDGE,"E9.0.2.18"),sQuery(id+"F2.wireOp",EDGE,"E9.0.2.19"),sQuery(id+"F2.wireOp",EDGE,"E9.0.2.20"),sQuery(id+"F2.wireOp",EDGE,"E9.0.2.21"),sQuery(id+"F2.wireOp",EDGE,"E9.0.2.22"),sQuery(id+"F2.wireOp",EDGE,"E9.0.2.23"),sQuery(id+"F2.wireOp",EDGE,"E9.0.2.24"),sQuery(id+"F2.wireOp",EDGE,"E9.0.3.1"),sQuery(id+"F2.wireOp",EDGE,"E9.0.3.2"),sQuery(id+"F2.wireOp",EDGE,"E9.0.3.3"),sQuery(id+"F2.wireOp",EDGE,"E9.0.3.4"),sQuery(id+"F2.wireOp",EDGE,"E9.0.3.5"),sQuery(id+"F2.wireOp",EDGE,"E9.0.3.6"),sQuery(id+"F2.wireOp",EDGE,"E9.0.3.7"),sQuery(id+"F2.wireOp",EDGE,"E9.0.3.8"),sQuery(id+"F2.wireOp",EDGE,"E9.0.3.9"),sQuery(id+"F2.wireOp",EDGE,"E9.0.3.10"),sQuery(id+"F2.wireOp",EDGE,"E9.0.3.11"),sQuery(id+"F2.wireOp",EDGE,"E9.0.3.12"),sQuery(id+"F2.wireOp",EDGE,"E9.0.3.13"),sQuery(id+"F2.wireOp",EDGE,"E9.0.3.14"),sQuery(id+"F2.wireOp",EDGE,"E9.0.3.15"),sQuery(id+"F2.wireOp",EDGE,"E9.0.3.16"),sQuery(id+"F2.wireOp",EDGE,"E9.0.3.17"),sQuery(id+"F2.wireOp",EDGE,"E9.0.3.18"),sQuery(id+"F2.wireOp",EDGE,"E9.0.3.19"),sQuery(id+"F2.wireOp",EDGE,"E9.0.3.20"),sQuery(id+"F2.wireOp",EDGE,"E9.0.3.21"),sQuery(id+"F2.wireOp",EDGE,"E9.0.3.22"),sQuery(id+"F2.wireOp",EDGE,"E9.0.3.23"),sQuery(id+"F2.wireOp",EDGE,"E9.0.3.24"),sQuery(id+"F2.wireOp",EDGE,"E9.0.4.1"),sQuery(id+"F2.wireOp",EDGE,"E9.0.4.2"),sQuery(id+"F2.wireOp",EDGE,"E9.0.4.3"),sQuery(id+"F2.wireOp",EDGE,"E9.0.4.4"),sQuery(id+"F2.wireOp",EDGE,"E9.0.4.5"),sQuery(id+"F2.wireOp",EDGE,"E9.0.4.7"),sQuery(id+"F2.wireOp",EDGE,"E9.0.4.8"),sQuery(id+"F2.wireOp",EDGE,"E9.0.4.13"),sQuery(id+"F2.wireOp",EDGE,"E9.0.4.14"),sQuery(id+"F2.wireOp",EDGE,"E9.0.4.17"),sQuery(id+"F2.wireOp",EDGE,"E9.0.4.18"),sQuery(id+"F2.wireOp",EDGE,"E9.0.4.19"),sQuery(id+"F2.wireOp",EDGE,"E9.0.4.21"),sQuery(id+"F2.wireOp",EDGE,"E9.0.4.22"),sQuery(id+"F2.wireOp",EDGE,"E9.0.4.23"),sQuery(id+"F2.wireOp",EDGE,"E9.0.4.24"),sQuery(id+"F2.wireOp",EDGE,"E9.0.5.1"),sQuery(id+"F2.wireOp",EDGE,"E9.0.5.2"),sQuery(id+"F2.wireOp",EDGE,"E9.0.5.3"),sQuery(id+"F2.wireOp",EDGE,"E9.0.5.4"),sQuery(id+"F2.wireOp",EDGE,"E9.0.5.5"),sQuery(id+"F2.wireOp",EDGE,"E9.0.5.7"),sQuery(id+"F2.wireOp",EDGE,"E9.0.5.8"),sQuery(id+"F2.wireOp",EDGE,"E9.0.5.13"),sQuery(id+"F2.wireOp",EDGE,"E9.0.5.14"),sQuery(id+"F2.wireOp",EDGE,"E9.0.5.17"),sQuery(id+"F2.wireOp",EDGE,"E9.0.5.18"),sQuery(id+"F2.wireOp",EDGE,"E9.0.5.19"),sQuery(id+"F2.wireOp",EDGE,"E9.0.5.21"),sQuery(id+"F2.wireOp",EDGE,"E9.0.5.22"),sQuery(id+"F2.wireOp",EDGE,"E9.0.5.23"),sQuery(id+"F2.wireOp",EDGE,"E9.0.5.24")])],"isStart":false})]});
            var Q4;
            Q4=makeQuery(id+"F3.boolean.opBoolean","INTERSECT",EDGE,{"derivedFrom":[makeQuery(id+"F1.opExtrude","SWEPT_FACE",FACE,{"disambiguationData":[OSD([sQuery(id+"F0.wireOp",EDGE,"E4.4")])]}),makeQuery(id+"F3.opExtrude","CAP_FACE",FACE,{"disambiguationData":[OSD([sQuery(id+"F2.wireOp",EDGE,"E5.0.0"),sQuery(id+"F2.wireOp",EDGE,"E5.0.1"),sQuery(id+"F2.wireOp",EDGE,"E5.0.2"),sQuery(id+"F2.wireOp",EDGE,"E5.0.3"),sQuery(id+"F2.wireOp",EDGE,"E5.0.4"),sQuery(id+"F2.wireOp",EDGE,"E5.0.5"),sQuery(id+"F2.wireOp",EDGE,"E6.bottom"),sQuery(id+"F2.wireOp",EDGE,"E6.top"),sQuery(id+"F2.wireOp",EDGE,"E6.left"),sQuery(id+"F2.wireOp",EDGE,"E6.right"),sQuery(id+"F2.wireOp",EDGE,"E7.1.0.0"),sQuery(id+"F2.wireOp",EDGE,"E7.1.0.1"),sQuery(id+"F2.wireOp",EDGE,"E7.1.0.2"),sQuery(id+"F2.wireOp",EDGE,"E7.1.0.3"),sQuery(id+"F2.wireOp",EDGE,"E7.2.0.0"),sQuery(id+"F2.wireOp",EDGE,"E7.2.0.1"),sQuery(id+"F2.wireOp",EDGE,"E7.2.0.2"),sQuery(id+"F2.wireOp",EDGE,"E7.2.0.3"),sQuery(id+"F2.wireOp",EDGE,"E8.0.3.0"),sQuery(id+"F2.wireOp",EDGE,"E8.3.3.0"),sQuery(id+"F2.wireOp",EDGE,"E8.6.3.0"),sQuery(id+"F2.wireOp",EDGE,"E8.9.3.0"),sQuery(id+"F2.wireOp",EDGE,"E8.0.4.0"),sQuery(id+"F2.wireOp",EDGE,"E8.3.4.0"),sQuery(id+"F2.wireOp",EDGE,"E8.6.4.0"),sQuery(id+"F2.wireOp",EDGE,"E8.9.4.0"),sQuery(id+"F2.wireOp",EDGE,"E8.0.5.0"),sQuery(id+"F2.wireOp",EDGE,"E8.3.5.0"),sQuery(id+"F2.wireOp",EDGE,"E8.6.5.0"),sQuery(id+"F2.wireOp",EDGE,"E8.9.5.0"),sQuery(id+"F2.wireOp",EDGE,"E9.0.1.1"),sQuery(id+"F2.wireOp",EDGE,"E9.0.1.2"),sQuery(id+"F2.wireOp",EDGE,"E9.0.1.3"),sQuery(id+"F2.wireOp",EDGE,"E9.0.1.4"),sQuery(id+"F2.wireOp",EDGE,"E9.0.1.5"),sQuery(id+"F2.wireOp",EDGE,"E9.0.1.6"),sQuery(id+"F2.wireOp",EDGE,"E9.0.1.7"),sQuery(id+"F2.wireOp",EDGE,"E9.0.1.8"),sQuery(id+"F2.wireOp",EDGE,"E9.0.1.9"),sQuery(id+"F2.wireOp",EDGE,"E9.0.1.10"),sQuery(id+"F2.wireOp",EDGE,"E9.0.1.11"),sQuery(id+"F2.wireOp",EDGE,"E9.0.1.12"),sQuery(id+"F2.wireOp",EDGE,"E9.0.1.13"),sQuery(id+"F2.wireOp",EDGE,"E9.0.1.14"),sQuery(id+"F2.wireOp",EDGE,"E9.0.1.15"),sQuery(id+"F2.wireOp",EDGE,"E9.0.1.16"),sQuery(id+"F2.wireOp",EDGE,"E9.0.1.17"),sQuery(id+"F2.wireOp",EDGE,"E9.0.1.18"),sQuery(id+"F2.wireOp",EDGE,"E9.0.1.19"),sQuery(id+"F2.wireOp",EDGE,"E9.0.1.20"),sQuery(id+"F2.wireOp",EDGE,"E9.0.1.21"),sQuery(id+"F2.wireOp",EDGE,"E9.0.1.22"),sQuery(id+"F2.wireOp",EDGE,"E9.0.1.23"),sQuery(id+"F2.wireOp",EDGE,"E9.0.1.24"),sQuery(id+"F2.wireOp",EDGE,"E9.0.2.1"),sQuery(id+"F2.wireOp",EDGE,"E9.0.2.2"),sQuery(id+"F2.wireOp",EDGE,"E9.0.2.3"),sQuery(id+"F2.wireOp",EDGE,"E9.0.2.4"),sQuery(id+"F2.wireOp",EDGE,"E9.0.2.5"),sQuery(id+"F2.wireOp",EDGE,"E9.0.2.6"),sQuery(id+"F2.wireOp",EDGE,"E9.0.2.7"),sQuery(id+"F2.wireOp",EDGE,"E9.0.2.8"),sQuery(id+"F2.wireOp",EDGE,"E9.0.2.9"),sQuery(id+"F2.wireOp",EDGE,"E9.0.2.10"),sQuery(id+"F2.wireOp",EDGE,"E9.0.2.11"),sQuery(id+"F2.wireOp",EDGE,"E9.0.2.12"),sQuery(id+"F2.wireOp",EDGE,"E9.0.2.13"),sQuery(id+"F2.wireOp",EDGE,"E9.0.2.14"),sQuery(id+"F2.wireOp",EDGE,"E9.0.2.15"),sQuery(id+"F2.wireOp",EDGE,"E9.0.2.16"),sQuery(id+"F2.wireOp",EDGE,"E9.0.2.17"),sQuery(id+"F2.wireOp",EDGE,"E9.0.2.18"),sQuery(id+"F2.wireOp",EDGE,"E9.0.2.19"),sQuery(id+"F2.wireOp",EDGE,"E9.0.2.20"),sQuery(id+"F2.wireOp",EDGE,"E9.0.2.21"),sQuery(id+"F2.wireOp",EDGE,"E9.0.2.22"),sQuery(id+"F2.wireOp",EDGE,"E9.0.2.23"),sQuery(id+"F2.wireOp",EDGE,"E9.0.2.24"),sQuery(id+"F2.wireOp",EDGE,"E9.0.3.1"),sQuery(id+"F2.wireOp",EDGE,"E9.0.3.2"),sQuery(id+"F2.wireOp",EDGE,"E9.0.3.3"),sQuery(id+"F2.wireOp",EDGE,"E9.0.3.4"),sQuery(id+"F2.wireOp",EDGE,"E9.0.3.5"),sQuery(id+"F2.wireOp",EDGE,"E9.0.3.6"),sQuery(id+"F2.wireOp",EDGE,"E9.0.3.7"),sQuery(id+"F2.wireOp",EDGE,"E9.0.3.8"),sQuery(id+"F2.wireOp",EDGE,"E9.0.3.9"),sQuery(id+"F2.wireOp",EDGE,"E9.0.3.10"),sQuery(id+"F2.wireOp",EDGE,"E9.0.3.11"),sQuery(id+"F2.wireOp",EDGE,"E9.0.3.12"),sQuery(id+"F2.wireOp",EDGE,"E9.0.3.13"),sQuery(id+"F2.wireOp",EDGE,"E9.0.3.14"),sQuery(id+"F2.wireOp",EDGE,"E9.0.3.15"),sQuery(id+"F2.wireOp",EDGE,"E9.0.3.16"),sQuery(id+"F2.wireOp",EDGE,"E9.0.3.17"),sQuery(id+"F2.wireOp",EDGE,"E9.0.3.18"),sQuery(id+"F2.wireOp",EDGE,"E9.0.3.19"),sQuery(id+"F2.wireOp",EDGE,"E9.0.3.20"),sQuery(id+"F2.wireOp",EDGE,"E9.0.3.21"),sQuery(id+"F2.wireOp",EDGE,"E9.0.3.22"),sQuery(id+"F2.wireOp",EDGE,"E9.0.3.23"),sQuery(id+"F2.wireOp",EDGE,"E9.0.3.24"),sQuery(id+"F2.wireOp",EDGE,"E9.0.4.1"),sQuery(id+"F2.wireOp",EDGE,"E9.0.4.2"),sQuery(id+"F2.wireOp",EDGE,"E9.0.4.3"),sQuery(id+"F2.wireOp",EDGE,"E9.0.4.4"),sQuery(id+"F2.wireOp",EDGE,"E9.0.4.5"),sQuery(id+"F2.wireOp",EDGE,"E9.0.4.7"),sQuery(id+"F2.wireOp",EDGE,"E9.0.4.8"),sQuery(id+"F2.wireOp",EDGE,"E9.0.4.13"),sQuery(id+"F2.wireOp",EDGE,"E9.0.4.14"),sQuery(id+"F2.wireOp",EDGE,"E9.0.4.17"),sQuery(id+"F2.wireOp",EDGE,"E9.0.4.18"),sQuery(id+"F2.wireOp",EDGE,"E9.0.4.19"),sQuery(id+"F2.wireOp",EDGE,"E9.0.4.21"),sQuery(id+"F2.wireOp",EDGE,"E9.0.4.22"),sQuery(id+"F2.wireOp",EDGE,"E9.0.4.23"),sQuery(id+"F2.wireOp",EDGE,"E9.0.4.24"),sQuery(id+"F2.wireOp",EDGE,"E9.0.5.1"),sQuery(id+"F2.wireOp",EDGE,"E9.0.5.2"),sQuery(id+"F2.wireOp",EDGE,"E9.0.5.3"),sQuery(id+"F2.wireOp",EDGE,"E9.0.5.4"),sQuery(id+"F2.wireOp",EDGE,"E9.0.5.5"),sQuery(id+"F2.wireOp",EDGE,"E9.0.5.7"),sQuery(id+"F2.wireOp",EDGE,"E9.0.5.8"),sQuery(id+"F2.wireOp",EDGE,"E9.0.5.13"),sQuery(id+"F2.wireOp",EDGE,"E9.0.5.14"),sQuery(id+"F2.wireOp",EDGE,"E9.0.5.17"),sQuery(id+"F2.wireOp",EDGE,"E9.0.5.18"),sQuery(id+"F2.wireOp",EDGE,"E9.0.5.19"),sQuery(id+"F2.wireOp",EDGE,"E9.0.5.21"),sQuery(id+"F2.wireOp",EDGE,"E9.0.5.22"),sQuery(id+"F2.wireOp",EDGE,"E9.0.5.23"),sQuery(id+"F2.wireOp",EDGE,"E9.0.5.24")])],"isStart":false})]});
            var Q5;
            Q5=makeQuery(id+"F3.boolean.opBoolean","INTERSECT",EDGE,{"derivedFrom":[makeQuery(id+"F1.opExtrude","SWEPT_FACE",FACE,{"disambiguationData":[OSD([sQuery(id+"F0.wireOp",EDGE,"E4.2")])]}),makeQuery(id+"F3.opExtrude","CAP_FACE",FACE,{"disambiguationData":[OSD([sQuery(id+"F2.wireOp",EDGE,"E5.0.0"),sQuery(id+"F2.wireOp",EDGE,"E5.0.1"),sQuery(id+"F2.wireOp",EDGE,"E5.0.2"),sQuery(id+"F2.wireOp",EDGE,"E5.0.3"),sQuery(id+"F2.wireOp",EDGE,"E5.0.4"),sQuery(id+"F2.wireOp",EDGE,"E5.0.5"),sQuery(id+"F2.wireOp",EDGE,"E6.bottom"),sQuery(id+"F2.wireOp",EDGE,"E6.top"),sQuery(id+"F2.wireOp",EDGE,"E6.left"),sQuery(id+"F2.wireOp",EDGE,"E6.right"),sQuery(id+"F2.wireOp",EDGE,"E7.1.0.0"),sQuery(id+"F2.wireOp",EDGE,"E7.1.0.1"),sQuery(id+"F2.wireOp",EDGE,"E7.1.0.2"),sQuery(id+"F2.wireOp",EDGE,"E7.1.0.3"),sQuery(id+"F2.wireOp",EDGE,"E7.2.0.0"),sQuery(id+"F2.wireOp",EDGE,"E7.2.0.1"),sQuery(id+"F2.wireOp",EDGE,"E7.2.0.2"),sQuery(id+"F2.wireOp",EDGE,"E7.2.0.3"),sQuery(id+"F2.wireOp",EDGE,"E8.0.3.0"),sQuery(id+"F2.wireOp",EDGE,"E8.3.3.0"),sQuery(id+"F2.wireOp",EDGE,"E8.6.3.0"),sQuery(id+"F2.wireOp",EDGE,"E8.9.3.0"),sQuery(id+"F2.wireOp",EDGE,"E8.0.4.0"),sQuery(id+"F2.wireOp",EDGE,"E8.3.4.0"),sQuery(id+"F2.wireOp",EDGE,"E8.6.4.0"),sQuery(id+"F2.wireOp",EDGE,"E8.9.4.0"),sQuery(id+"F2.wireOp",EDGE,"E8.0.5.0"),sQuery(id+"F2.wireOp",EDGE,"E8.3.5.0"),sQuery(id+"F2.wireOp",EDGE,"E8.6.5.0"),sQuery(id+"F2.wireOp",EDGE,"E8.9.5.0"),sQuery(id+"F2.wireOp",EDGE,"E9.0.1.1"),sQuery(id+"F2.wireOp",EDGE,"E9.0.1.2"),sQuery(id+"F2.wireOp",EDGE,"E9.0.1.3"),sQuery(id+"F2.wireOp",EDGE,"E9.0.1.4"),sQuery(id+"F2.wireOp",EDGE,"E9.0.1.5"),sQuery(id+"F2.wireOp",EDGE,"E9.0.1.6"),sQuery(id+"F2.wireOp",EDGE,"E9.0.1.7"),sQuery(id+"F2.wireOp",EDGE,"E9.0.1.8"),sQuery(id+"F2.wireOp",EDGE,"E9.0.1.9"),sQuery(id+"F2.wireOp",EDGE,"E9.0.1.10"),sQuery(id+"F2.wireOp",EDGE,"E9.0.1.11"),sQuery(id+"F2.wireOp",EDGE,"E9.0.1.12"),sQuery(id+"F2.wireOp",EDGE,"E9.0.1.13"),sQuery(id+"F2.wireOp",EDGE,"E9.0.1.14"),sQuery(id+"F2.wireOp",EDGE,"E9.0.1.15"),sQuery(id+"F2.wireOp",EDGE,"E9.0.1.16"),sQuery(id+"F2.wireOp",EDGE,"E9.0.1.17"),sQuery(id+"F2.wireOp",EDGE,"E9.0.1.18"),sQuery(id+"F2.wireOp",EDGE,"E9.0.1.19"),sQuery(id+"F2.wireOp",EDGE,"E9.0.1.20"),sQuery(id+"F2.wireOp",EDGE,"E9.0.1.21"),sQuery(id+"F2.wireOp",EDGE,"E9.0.1.22"),sQuery(id+"F2.wireOp",EDGE,"E9.0.1.23"),sQuery(id+"F2.wireOp",EDGE,"E9.0.1.24"),sQuery(id+"F2.wireOp",EDGE,"E9.0.2.1"),sQuery(id+"F2.wireOp",EDGE,"E9.0.2.2"),sQuery(id+"F2.wireOp",EDGE,"E9.0.2.3"),sQuery(id+"F2.wireOp",EDGE,"E9.0.2.4"),sQuery(id+"F2.wireOp",EDGE,"E9.0.2.5"),sQuery(id+"F2.wireOp",EDGE,"E9.0.2.6"),sQuery(id+"F2.wireOp",EDGE,"E9.0.2.7"),sQuery(id+"F2.wireOp",EDGE,"E9.0.2.8"),sQuery(id+"F2.wireOp",EDGE,"E9.0.2.9"),sQuery(id+"F2.wireOp",EDGE,"E9.0.2.10"),sQuery(id+"F2.wireOp",EDGE,"E9.0.2.11"),sQuery(id+"F2.wireOp",EDGE,"E9.0.2.12"),sQuery(id+"F2.wireOp",EDGE,"E9.0.2.13"),sQuery(id+"F2.wireOp",EDGE,"E9.0.2.14"),sQuery(id+"F2.wireOp",EDGE,"E9.0.2.15"),sQuery(id+"F2.wireOp",EDGE,"E9.0.2.16"),sQuery(id+"F2.wireOp",EDGE,"E9.0.2.17"),sQuery(id+"F2.wireOp",EDGE,"E9.0.2.18"),sQuery(id+"F2.wireOp",EDGE,"E9.0.2.19"),sQuery(id+"F2.wireOp",EDGE,"E9.0.2.20"),sQuery(id+"F2.wireOp",EDGE,"E9.0.2.21"),sQuery(id+"F2.wireOp",EDGE,"E9.0.2.22"),sQuery(id+"F2.wireOp",EDGE,"E9.0.2.23"),sQuery(id+"F2.wireOp",EDGE,"E9.0.2.24"),sQuery(id+"F2.wireOp",EDGE,"E9.0.3.1"),sQuery(id+"F2.wireOp",EDGE,"E9.0.3.2"),sQuery(id+"F2.wireOp",EDGE,"E9.0.3.3"),sQuery(id+"F2.wireOp",EDGE,"E9.0.3.4"),sQuery(id+"F2.wireOp",EDGE,"E9.0.3.5"),sQuery(id+"F2.wireOp",EDGE,"E9.0.3.6"),sQuery(id+"F2.wireOp",EDGE,"E9.0.3.7"),sQuery(id+"F2.wireOp",EDGE,"E9.0.3.8"),sQuery(id+"F2.wireOp",EDGE,"E9.0.3.9"),sQuery(id+"F2.wireOp",EDGE,"E9.0.3.10"),sQuery(id+"F2.wireOp",EDGE,"E9.0.3.11"),sQuery(id+"F2.wireOp",EDGE,"E9.0.3.12"),sQuery(id+"F2.wireOp",EDGE,"E9.0.3.13"),sQuery(id+"F2.wireOp",EDGE,"E9.0.3.14"),sQuery(id+"F2.wireOp",EDGE,"E9.0.3.15"),sQuery(id+"F2.wireOp",EDGE,"E9.0.3.16"),sQuery(id+"F2.wireOp",EDGE,"E9.0.3.17"),sQuery(id+"F2.wireOp",EDGE,"E9.0.3.18"),sQuery(id+"F2.wireOp",EDGE,"E9.0.3.19"),sQuery(id+"F2.wireOp",EDGE,"E9.0.3.20"),sQuery(id+"F2.wireOp",EDGE,"E9.0.3.21"),sQuery(id+"F2.wireOp",EDGE,"E9.0.3.22"),sQuery(id+"F2.wireOp",EDGE,"E9.0.3.23"),sQuery(id+"F2.wireOp",EDGE,"E9.0.3.24"),sQuery(id+"F2.wireOp",EDGE,"E9.0.4.1"),sQuery(id+"F2.wireOp",EDGE,"E9.0.4.2"),sQuery(id+"F2.wireOp",EDGE,"E9.0.4.3"),sQuery(id+"F2.wireOp",EDGE,"E9.0.4.4"),sQuery(id+"F2.wireOp",EDGE,"E9.0.4.5"),sQuery(id+"F2.wireOp",EDGE,"E9.0.4.7"),sQuery(id+"F2.wireOp",EDGE,"E9.0.4.8"),sQuery(id+"F2.wireOp",EDGE,"E9.0.4.13"),sQuery(id+"F2.wireOp",EDGE,"E9.0.4.14"),sQuery(id+"F2.wireOp",EDGE,"E9.0.4.17"),sQuery(id+"F2.wireOp",EDGE,"E9.0.4.18"),sQuery(id+"F2.wireOp",EDGE,"E9.0.4.19"),sQuery(id+"F2.wireOp",EDGE,"E9.0.4.21"),sQuery(id+"F2.wireOp",EDGE,"E9.0.4.22"),sQuery(id+"F2.wireOp",EDGE,"E9.0.4.23"),sQuery(id+"F2.wireOp",EDGE,"E9.0.4.24"),sQuery(id+"F2.wireOp",EDGE,"E9.0.5.1"),sQuery(id+"F2.wireOp",EDGE,"E9.0.5.2"),sQuery(id+"F2.wireOp",EDGE,"E9.0.5.3"),sQuery(id+"F2.wireOp",EDGE,"E9.0.5.4"),sQuery(id+"F2.wireOp",EDGE,"E9.0.5.5"),sQuery(id+"F2.wireOp",EDGE,"E9.0.5.7"),sQuery(id+"F2.wireOp",EDGE,"E9.0.5.8"),sQuery(id+"F2.wireOp",EDGE,"E9.0.5.13"),sQuery(id+"F2.wireOp",EDGE,"E9.0.5.14"),sQuery(id+"F2.wireOp",EDGE,"E9.0.5.17"),sQuery(id+"F2.wireOp",EDGE,"E9.0.5.18"),sQuery(id+"F2.wireOp",EDGE,"E9.0.5.19"),sQuery(id+"F2.wireOp",EDGE,"E9.0.5.21"),sQuery(id+"F2.wireOp",EDGE,"E9.0.5.22"),sQuery(id+"F2.wireOp",EDGE,"E9.0.5.23"),sQuery(id+"F2.wireOp",EDGE,"E9.0.5.24")])],"isStart":false})]});
            fillet(context, id + "F8", {"entities" : qUnion([Q0, Q1, Q2, Q3, Q4, Q5]), "radius" : 9.52 * mm, "tangentPropagation" : true, "allowEdgeOverflow" : false});
        }
        {
            var Q0;
            Q0=makeQuery(id+"F1.opExtrude","SWEPT_EDGE",EDGE,{"disambiguationData":[OSD([sQuery(id+"F0.wireOp",EDGE,"E0.top"),sQuery(id+"F0.wireOp",EDGE,"E1")])]});
            var Q1;
            Q1=makeQuery(id+"F1.opExtrude","SWEPT_EDGE",EDGE,{"disambiguationData":[OSD([sQuery(id+"F0.wireOp",EDGE,"E0.left"),sQuery(id+"F0.wireOp",EDGE,"E2")])]});
            var Q2;
            Q2=makeQuery(id+"F1.opExtrude","SWEPT_EDGE",EDGE,{"disambiguationData":[OSD([sQuery(id+"F0.wireOp",EDGE,"E0.bottom"),sQuery(id+"F0.wireOp",EDGE,"E0.left")])]});
            var Q3;
            Q3=makeQuery(id+"F1.opExtrude","SWEPT_EDGE",EDGE,{"disambiguationData":[OSD([sQuery(id+"F0.wireOp",EDGE,"E0.bottom"),sQuery(id+"F0.wireOp",EDGE,"E0.right")])]});
            var Q4;
            Q4=makeQuery(id+"F1.opExtrude","SWEPT_EDGE",EDGE,{"disambiguationData":[OSD([sQuery(id+"F0.wireOp",EDGE,"E0.top"),sQuery(id+"F0.wireOp",EDGE,"E0.right")])]});
            var Q5;
            Q5=makeQuery(id+"F1.opExtrude","SWEPT_EDGE",EDGE,{"disambiguationData":[OSD([sQuery(id+"F0.wireOp",EDGE,"E4.4"),sQuery(id+"F0.wireOp",EDGE,"E4.5")])]});
            fillet(context, id + "F9", {"entities" : qUnion([Q0, Q1, Q2, Q3, Q4, Q5]), "radius" : 6.35 * mm, "tangentPropagation" : true, "allowEdgeOverflow" : false});
        }
        {
            var Q0;
            Q0=makeQuery(id+"F1.opExtrude","SWEPT_EDGE",EDGE,{"disambiguationData":[OSD([sQuery(id+"F0.wireOp",EDGE,"E4.0"),sQuery(id+"F0.wireOp",EDGE,"E4.3")])]});
            var Q1;
            Q1=makeQuery(id+"F1.opExtrude","SWEPT_EDGE",EDGE,{"disambiguationData":[OSD([sQuery(id+"F0.wireOp",EDGE,"E4.0"),sQuery(id+"F0.wireOp",EDGE,"E4.5")])]});
            var Q2;
            Q2=makeQuery(id+"F1.opExtrude","SWEPT_EDGE",EDGE,{"disambiguationData":[OSD([sQuery(id+"F0.wireOp",EDGE,"E4.2"),sQuery(id+"F0.wireOp",EDGE,"E4.4")])]});
            var Q3;
            Q3=makeQuery(id+"F1.opExtrude","SWEPT_EDGE",EDGE,{"disambiguationData":[OSD([sQuery(id+"F0.wireOp",EDGE,"E4.1"),sQuery(id+"F0.wireOp",EDGE,"E4.2")])]});
            var Q4;
            Q4=makeQuery(id+"F1.opExtrude","SWEPT_EDGE",EDGE,{"disambiguationData":[OSD([sQuery(id+"F0.wireOp",EDGE,"E4.1"),sQuery(id+"F0.wireOp",EDGE,"E4.3")])]});
            var Q5;
            Q5=makeQuery(id+"F1.opExtrude","SWEPT_EDGE",EDGE,{"disambiguationData":[OSD([sQuery(id+"F0.wireOp",EDGE,"E1"),sQuery(id+"F0.wireOp",EDGE,"E2")])]});
            fillet(context, id + "F10", {"entities" : qUnion([Q0, Q1, Q2, Q3, Q4, Q5]), "radius" : 3.17 * mm, "tangentPropagation" : true, "allowEdgeOverflow" : false});
        }
        {
            var Q0;
            Q0=makeQuery(id+"F1.opExtrude","CAP_EDGE",EDGE,{"disambiguationData":[OSD([sQuery(id+"F0.wireOp",EDGE,"E0.right")])],"isStart":true});
            fillet(context, id + "F11", {"entities" : qUnion([Q0]), "radius" : 12.7 * mm, "tangentPropagation" : true, "allowEdgeOverflow" : false});
        }
    });
